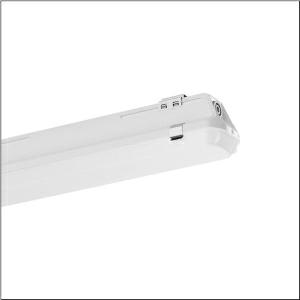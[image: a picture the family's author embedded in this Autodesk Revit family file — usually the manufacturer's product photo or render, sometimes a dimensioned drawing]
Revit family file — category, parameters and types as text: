
# Revit family: monsun_r__11_51fp20dp460h_2810
name_source: partatom
category: Lighting Fixtures
units: mm (PartAtom-declared; Revit-internal decimal feet)

## family parameters
Cut with Voids When Loaded = No
Host = Face
Light Source = No
Part Type = Normal
Room Calculation Point = No
Round Connector Dimension = Use Diameter
Shared = No

## types (1)
- --- (1 x LED, 5450 lm, 34.6 W, 4000K)
    Apparent Load = 35 VA
    CIE Flux Codes = 45 75 93 94 100
    Color Rendering = 80
    Color Temperature = 4000K
    Default Elevation = 1800 mm
    Description = Monsun® 11, damp-proof luminaire, chain hanger, primary optical cover: enclosure, of PC, light emission: direct distribution, primary light characteristic: symmetric, installation type: suspended mounting, surface-mounted, horizontal mounting, vertical mounting, LED, rated luminous flux: 5.450lm, luminous efficacy: 158lm/W, light colour: 840, colour temperature: 4000K, control gear: ECG DALI, with terminal, 5-pole, max. 2.5mm², mains connection: 220..240V, AC, 50/60Hz, rated input power: 35W, luminaire housing, of glass-fibre reinforced polyester, uncoated, bright grey, incl. chain hanger, length: 1.590mm, width: 90mm, height: 88mm, clip for enclosure, of stainless steel (V2A), ceiling mounting element, of stainless steel (V2A), chain hanger, of stainless steel (V2A), protection rating (complete): IP66, insulation class (complete): insulation class I (protective earthing), certification: CE, ENEC, VDE, UKCA, protection symbol: D, impact resistance: IK08, permissible operating ambient temperature: -35..+40°C, standard: EN 50419, EN 60598-2-1, no direct snow, no direct sun, no direct rain, for indoor or canopied outdoor use, corresponds to IFS (International Featured Standards) requirements for safety and quality in the food industry, contact your sales advisor before using the luminaires in applications with unclear chemical exposure, large temperature fluctuations or condensation-forming humidity, LABS conformity tested according to VDMA 24364:2018-05, packaging unit: 1 piece
    Height = 89 mm
    Lamp = 1 x LED
    Lamp Light Flux = 5450 lm
    Lamp Power = 34.6 W
    Lamp count = 1
    Length = 1590 mm
    Luminous efficacy = 158 lm/W
    Manufacturer = Siteco
    ModVariant = No
    Model = 51FP20DP460H
    Mounting Place = Ceiling
    Mounting Type = Surface mounted
    Number of Poles = 1
    OnlyDefault = Yes
    Power Factor = 1
    Product Name = Monsun® 11
    Product group = damp-proof luminaire
    ProductGroupID = 301
    Protection Class = Protection class I
    Protection Degree = IP 66
    RLX_Detail_Level = 1
    RLX_Emergency_Light_Flux = 0 lm
    RLX_Emergency_Type = 0
    RLX_Emergency_Type_DB = No
    RlxData = <blob elided: 92393 chars, md5=5fba6ac1>
    Socket = socket
    Standby Power = 0 W
    System Light Flux = 5450 lm
    System Power = 35 W
    Type Comments = factory setting: luminous flux: 100 % | dim-lin: 254 | 232 mA
    Type Image = l_1004748.jpg
    URL = http://relux.com
    VarID = @adj_156531
    Voltage = 0 V
    Weight = 0.00 kg
    Width = 90 mm

## geometry (parser evidence)
native form markers: Blend x4, Sweep x16
no freeform markers — native parametric forms only
